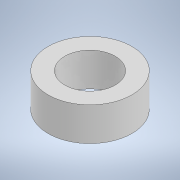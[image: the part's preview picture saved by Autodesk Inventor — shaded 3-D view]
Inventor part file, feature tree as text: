
AUTODESK INVENTOR PART (.ipt)
format: ipt  version: 2021.1 (Build 251245010, 245A)  size: 96,768 bytes
history: native  units: mm
features: other x1, extrude x1, sketch x1
ambient origin geometry x8: Origin, YZ Plane, XZ Plane, XY Plane, X Axis, Y Axis, Z Axis, Center Point
bodies: Body1 (feature_tree)
feature tree (3):
  other  "Твердое тело1"
  extrude  "Выдавливание1"  Depth=25.0mm
  sketch  "Эскиз1"
